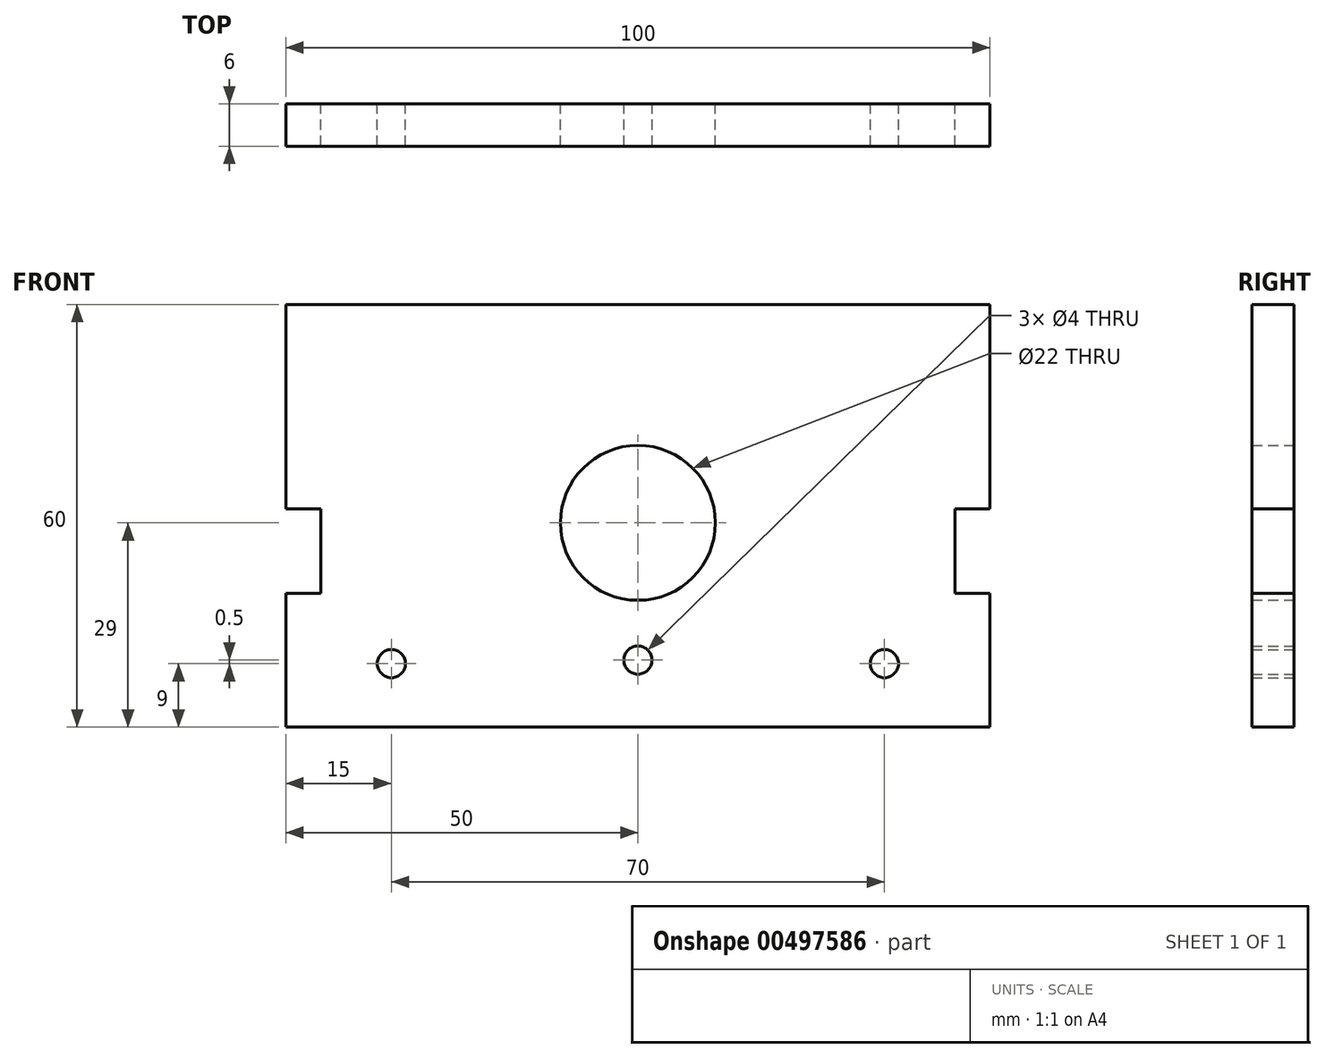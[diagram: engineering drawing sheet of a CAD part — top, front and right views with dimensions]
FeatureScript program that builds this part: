
annotation { "Feature Type Name" : "Feature", "Feature Type Description" : "" }
export const myFeature = defineFeature(function(context is Context, id is Id, definition is map)
    precondition{}
    {
        {
            var Q0;
            Q0=qCreatedBy(makeId("Front.planeOp"),FACE);
            var sketch = newSketch(context, id + "F0", { "sketchPlane" : qUnion([Q0])});
            skLineSegment(sketch, "E0.bottom", {"start": v(0, 60) * mm, "end": v(100, 60) * mm});
            skLineSegment(sketch, "E0.top", {"start": v(0, 0) * mm, "end": v(100, 0) * mm});
            skLineSegment(sketch, "E0.left", {"start": v(0, 60) * mm, "end": v(0, 0) * mm});
            skLineSegment(sketch, "E0.right", {"start": v(100, 60) * mm, "end": v(100, 0) * mm});
            skPoint(sketch, "E1.centerSnap0", {"position": v(0, 30) * mm});
            skCircle(sketch, "E2", {"center": v(50, 29) * mm, "radius": 11 * mm});
            skCircle(sketch, "E3", {"center": v(15, 9) * mm, "radius": 2 * mm});
            skLineSegment(sketch, "E4", {"start": v(50, 60) * mm, "end": v(50, 0) * mm, "construction": true});
            skCircle(sketch, "E5.MirrorC", {"center": v(85, 9) * mm, "radius": 2 * mm});
            skLineSegment(sketch, "E6.bottom", {"start": v(100, 19) * mm, "end": v(95, 19) * mm});
            skLineSegment(sketch, "E6.top", {"start": v(100, 31) * mm, "end": v(95, 31) * mm});
            skLineSegment(sketch, "E6.left", {"start": v(100, 19) * mm, "end": v(100, 31) * mm});
            skLineSegment(sketch, "E6.right", {"start": v(95, 19) * mm, "end": v(95, 31) * mm});
            skLineSegment(sketch, "E7.bottom", {"start": v(0, 19) * mm, "end": v(5, 19) * mm});
            skLineSegment(sketch, "E7.top", {"start": v(0, 31) * mm, "end": v(5, 31) * mm});
            skLineSegment(sketch, "E7.left", {"start": v(0, 19) * mm, "end": v(0, 31) * mm});
            skLineSegment(sketch, "E7.right", {"start": v(5, 19) * mm, "end": v(5, 31) * mm});
            skCircle(sketch, "E8", {"center": v(50, 29) * mm, "radius": 9.5 * mm, "construction": true});
            skCircle(sketch, "E9", {"center": v(50, 9.5) * mm, "radius": 2 * mm});
            skSolve(sketch);
        }
        {
            var Q0;
            Q0=makeQuery(id+"F0.imprint","IMPRINT",FACE,{"disambiguationData":[TD([[makeQuery(id+"F0.imprint","IMPRINT",EDGE,{"derivedFrom":sQuery(id+"F0.wireOp",EDGE,"E0.bottom")}),-1.0]])]});
            extrude(context, id + "F1", {"entities" : qUnion([Q0]), "depth" : 6 * mm});
        }
    });
